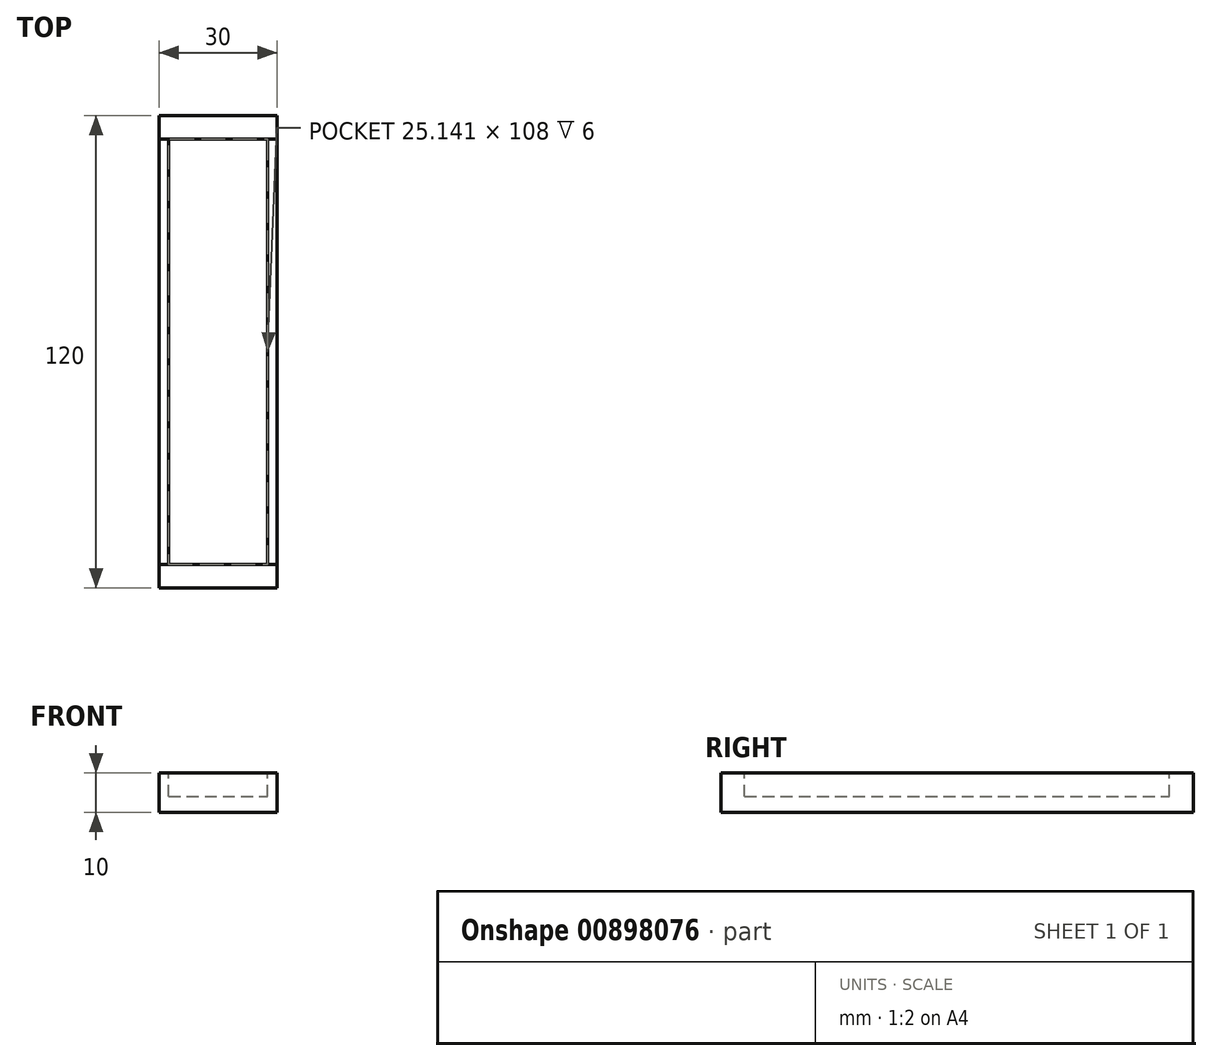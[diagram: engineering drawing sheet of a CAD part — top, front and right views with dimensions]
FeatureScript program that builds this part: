
annotation { "Feature Type Name" : "Feature", "Feature Type Description" : "" }
export const myFeature = defineFeature(function(context is Context, id is Id, definition is map)
    precondition{}
    {
        {
            var Q0;
            Q0=qCreatedBy(makeId("Front.planeOp"),FACE);
            var sketch = newSketch(context, id + "F0", { "sketchPlane" : qUnion([Q0])});
            skLineSegment(sketch, "E0.bottom", {"start": v(15, -5) * mm, "end": v(-15, -5) * mm});
            skLineSegment(sketch, "E0.top", {"start": v(15, 5) * mm, "end": v(-15, 5) * mm});
            skLineSegment(sketch, "E0.left", {"start": v(15, -5) * mm, "end": v(15, 5) * mm});
            skLineSegment(sketch, "E0.right", {"start": v(-15, -5) * mm, "end": v(-15, 5) * mm});
            skPoint(sketch, "E0.middle", {"position": v(0, 0) * mm});
            skLineSegment(sketch, "E1.bottom", {"start": v(-15, 5) * mm, "end": v(15, 5) * mm});
            skLineSegment(sketch, "E1.top", {"start": v(-7.14, 25) * mm, "end": v(-4, 25) * mm});
            skLineSegment(sketch, "E2", {"start": v(-7.14, 25) * mm, "end": v(-15, 5) * mm});
            skLineSegment(sketch, "E3", {"start": v(7.14, 25) * mm, "end": v(15, 5) * mm});
            skPoint(sketch, "E4.orphan", {"position": v(15, 25) * mm});
            skPoint(sketch, "E1.left.end.orphan", {"position": v(-15, 25) * mm});
            skPoint(sketch, "E5.center.orphan", {"position": v(0, 25) * mm});
            skLineSegment(sketch, "E6.bottom", {"start": v(4, 10) * mm, "end": v(-4, 10) * mm});
            skLineSegment(sketch, "E6.left", {"start": v(4, 10) * mm, "end": v(4, 25) * mm});
            skLineSegment(sketch, "E6.right", {"start": v(-4, 10) * mm, "end": v(-4, 25) * mm});
            skPoint(sketch, "E7.orphan", {"position": v(4, 40) * mm});
            skPoint(sketch, "E8.orphan", {"position": v(-4, 40) * mm});
            skLineSegment(sketch, "E9.trimOffspring", {"start": v(4, 25) * mm, "end": v(7.14, 25) * mm});
            skSolve(sketch);
        }
        {
            var Q0;
            Q0=makeQuery(id+"F0.imprint","IMPRINT",FACE,{"disambiguationData":[TD([[makeQuery(id+"F0.imprint","IMPRINT",EDGE,{"derivedFrom":sQuery(id+"F0.wireOp",EDGE,"E1.bottom")}),1.0]])]});
            var Q1;
            Q1=makeQuery(id+"F0.imprint","IMPRINT",FACE,{"disambiguationData":[TD([[makeQuery(id+"F0.imprint","IMPRINT",EDGE,{"derivedFrom":sQuery(id+"F0.wireOp",EDGE,"E0.bottom")}),-1.0]])]});
            extrude(context, id + "F1", {"entities" : qUnion([Q0, Q1]), "endBound" : BoundingType.SYMMETRIC, "depth" : 120 * mm, "offsetDistance" : 25 * mm});
        }
        {
            var Q0;
            Q0=qCreatedBy(makeId("Right.planeOp"),FACE);
            var sketch = newSketch(context, id + "F2", { "sketchPlane" : qUnion([Q0])});
            skLineSegment(sketch, "E10.bottom", {"start": v(54, 4.99) * mm, "end": v(-54, 4.99) * mm});
            skLineSegment(sketch, "E10.top", {"start": v(54, 44.91) * mm, "end": v(-54, 44.91) * mm});
            skLineSegment(sketch, "E10.left", {"start": v(54, 4.99) * mm, "end": v(54, 44.91) * mm});
            skLineSegment(sketch, "E10.right", {"start": v(-54, 4.99) * mm, "end": v(-54, 44.91) * mm});
            skPoint(sketch, "E10.middle", {"position": v(0, 24.95) * mm});
            skSolve(sketch);
        }
        {
            var Q0;
            Q0=makeQuery(id+"F2.imprint","IMPRINT",FACE,{"disambiguationData":[TD([[makeQuery(id+"F2.imprint","IMPRINT",EDGE,{"derivedFrom":sQuery(id+"F2.wireOp",EDGE,"E10.bottom")}),-1.0]])]});
            extrude(context, id + "F3", {"entities" : qUnion([Q0]), "operationType" : NewBodyOperationType.REMOVE, "endBound" : BoundingType.SYMMETRIC, "oppositeDirection" : true, "depth" : 300 * mm, "offsetDistance" : 25 * mm});
        }
        {
            var Q0;
            Q0=makeQuery(id+"F3.boolean.opBoolean","COPY",FACE,{"derivedFrom":makeQuery(id+"F3.opExtrude","SWEPT_FACE",FACE,{"disambiguationData":[OSD([sQuery(id+"F2.wireOp",EDGE,"E10.bottom")])]})});
            var sketch = newSketch(context, id + "F4", { "sketchPlane" : qUnion([Q0])});
            skLineSegment(sketch, "E11.bottom", {"start": v(12.57, -54) * mm, "end": v(-12.57, -54) * mm});
            skLineSegment(sketch, "E11.top", {"start": v(12.57, 54) * mm, "end": v(-12.57, 54) * mm});
            skLineSegment(sketch, "E11.left", {"start": v(12.57, -54) * mm, "end": v(12.57, 54) * mm});
            skLineSegment(sketch, "E11.right", {"start": v(-12.57, -54) * mm, "end": v(-12.57, 54) * mm});
            skPoint(sketch, "E11.middle", {"position": v(0, 0) * mm});
            skSolve(sketch);
        }
        {
            var Q0;
            Q0 = qSketchRegion(id + "F4", true);
            extrude(context, id + "F5", {"entities" : qUnion([Q0]), "operationType" : NewBodyOperationType.REMOVE, "oppositeDirection" : true, "depth" : 6 * mm, "offsetDistance" : 25 * mm});
        }
    });
